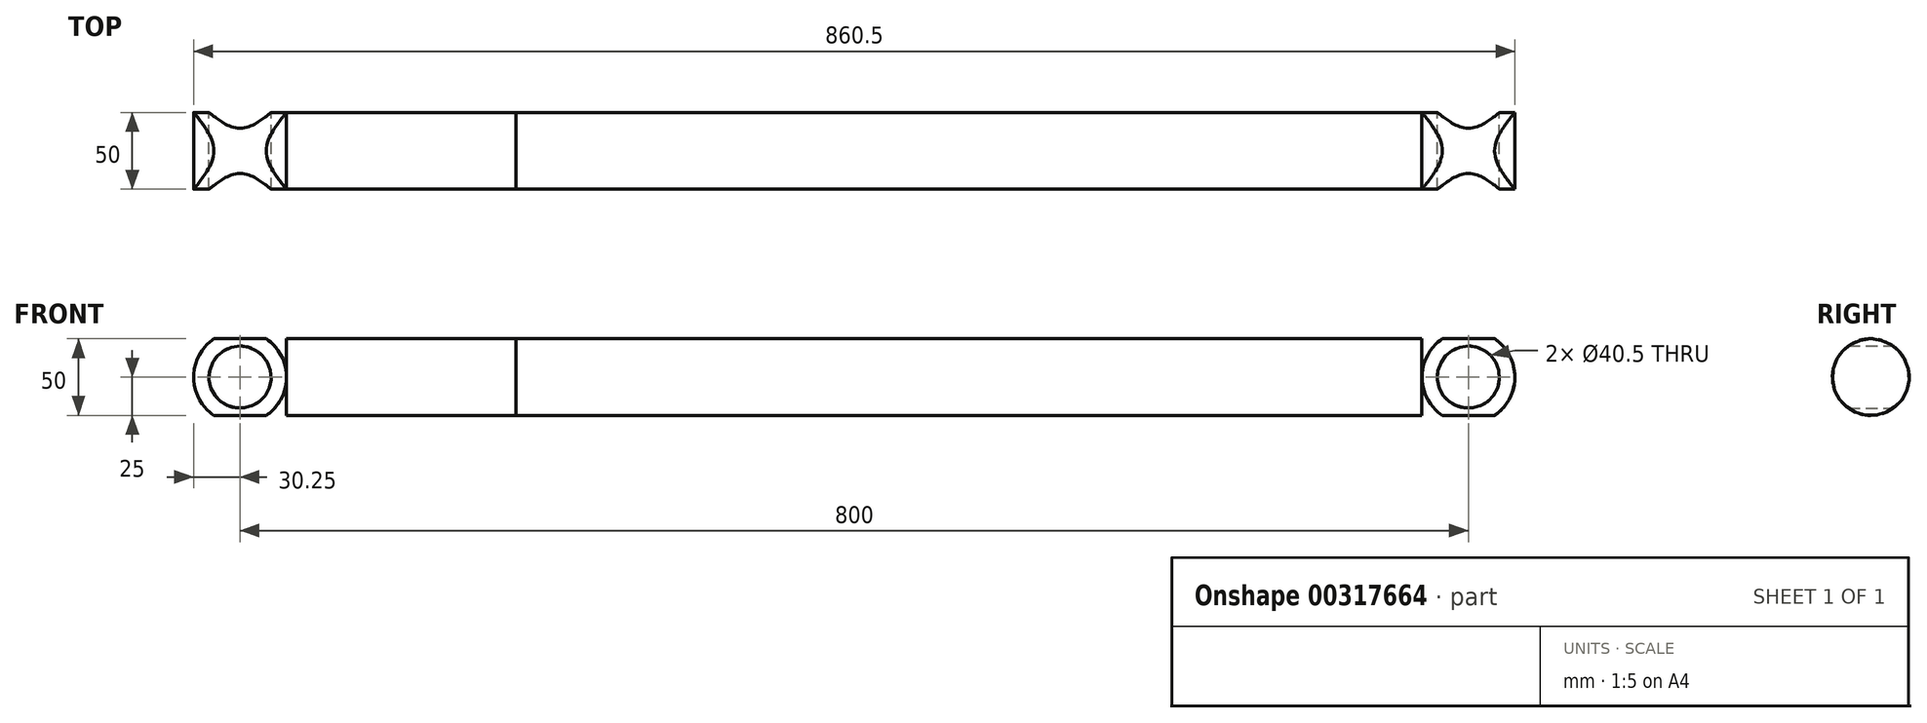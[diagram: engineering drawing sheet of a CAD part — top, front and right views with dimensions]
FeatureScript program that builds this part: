
annotation { "Feature Type Name" : "Feature", "Feature Type Description" : "" }
export const myFeature = defineFeature(function(context is Context, id is Id, definition is map)
    precondition{}
    {
        {
            assignVariable(context, id + "F0", {"name" : "Interasse_pistone", "anyValue" : 800});
        }
        {
            assignVariable(context, id + "F1", {"name" : "Corsa_persa", "anyValue" : 230});
        }
        {
            var Q0;
            Q0=qCreatedBy(makeId("Front.planeOp"),FACE);
            var sketch = newSketch(context, id + "F2", { "sketchPlane" : qUnion([Q0])});
            skCircle(sketch, "E0", {"center": v(0, 0) * mm, "radius": 20.25 * mm});
            skCircle(sketch, "E1.0", {"center": v(0, 0) * mm, "radius": 30.25 * mm});
            skLineSegment(sketch, "E2", {"start": v(0, 0) * mm, "end": v(30.25, 0) * mm, "construction": true});
            skLineSegment(sketch, "E3.bottom", {"start": v(30.25, 50) * mm, "end": v(749.75, 50) * mm});
            skLineSegment(sketch, "E3.top", {"start": v(30.25, -50) * mm, "end": v(749.75, -50) * mm});
            skLineSegment(sketch, "E3.left", {"start": v(30.25, 50) * mm, "end": v(30.25, -50) * mm});
            skLineSegment(sketch, "E3.right", {"start": v(749.75, 50) * mm, "end": v(749.75, -50) * mm});
            skLineSegment(sketch, "E4", {"start": v(30.25, 0) * mm, "end": v(749.75, 0) * mm, "construction": true});
            skCircle(sketch, "E5", {"center": v(800, 0) * mm, "radius": 20.25 * mm, "construction": true});
            skCircle(sketch, "E6.0", {"center": v(800, 0) * mm, "radius": 30.25 * mm, "construction": true});
            skLineSegment(sketch, "E7", {"start": v(769.75, 0) * mm, "end": v(830.25, 0) * mm, "construction": true});
            skLineSegment(sketch, "E8", {"start": v(800, 30.25) * mm, "end": v(800, -30.25) * mm, "construction": true});
            skLineSegment(sketch, "E9.bottom", {"start": v(830.25, 30.25) * mm, "end": v(769.75, 30.25) * mm, "construction": true});
            skLineSegment(sketch, "E9.top", {"start": v(830.25, -30.25) * mm, "end": v(769.75, -30.25) * mm, "construction": true});
            skLineSegment(sketch, "E9.left", {"start": v(830.25, 30.25) * mm, "end": v(830.25, -30.25) * mm, "construction": true});
            skLineSegment(sketch, "E9.right", {"start": v(769.75, 30.25) * mm, "end": v(769.75, -30.25) * mm, "construction": true});
            skSolve(sketch);
        }
        {
            var Q0;
            Q0=qCreatedBy(makeId("Right.planeOp"),FACE);
            var sketch = newSketch(context, id + "F3", { "sketchPlane" : qUnion([Q0])});
            skLineSegment(sketch, "E10.0", {"start": v(0, 50) * mm, "end": v(0, -50) * mm, "construction": true});
            skCircle(sketch, "E11", {"center": v(0, 0) * mm, "radius": 50 * mm});
            skSolve(sketch);
        }
        {
            var Q0;
            Q0=qCreatedBy(makeId("Right.planeOp"),FACE);
            var sketch = newSketch(context, id + "F4", { "sketchPlane" : qUnion([Q0])});
            skLineSegment(sketch, "E12.0", {"start": v(0, -30.25) * mm, "end": v(0, 30.25) * mm, "construction": true});
            skLineSegment(sketch, "E13.bottom", {"start": v(60, 30.25) * mm, "end": v(-60, 30.25) * mm});
            skLineSegment(sketch, "E13.top", {"start": v(60, -30.25) * mm, "end": v(-60, -30.25) * mm});
            skLineSegment(sketch, "E13.left", {"start": v(60, 30.25) * mm, "end": v(60, -30.25) * mm});
            skLineSegment(sketch, "E13.right", {"start": v(-60, 30.25) * mm, "end": v(-60, -30.25) * mm});
            skLineSegment(sketch, "E14", {"start": v(0, 30.25) * mm, "end": v(0, -30.25) * mm, "construction": true});
            skSolve(sketch);
        }
        {
            var Q0;
            Q0=qSketchRegion(id+"F2",true);
            extrude(context, id + "F5", {"entities" : qUnion([Q0]), "depth" : 1000 * mm, "hasSecondDirection" : true, "secondDirectionOppositeDirection" : true, "secondDirectionDepth" : 1000 * mm});
        }
        {
            var Q0;
            Q0=qSketchRegion(id+"F3",true);
            extrude(context, id + "F6", {"entities" : qUnion([Q0]), "operationType" : NewBodyOperationType.INTERSECT, "endBound" : BoundingType.THROUGH_ALL, "depth" : 25 * mm, "hasSecondDirection" : true, "secondDirectionBound" : SecondDirectionBoundingType.THROUGH_ALL, "secondDirectionOppositeDirection" : true, "secondDirectionDepth" : 25 * mm});
        }
        {
            var Q0;
            Q0=qSketchRegion(id+"F4",true);
            extrude(context, id + "F7", {"entities" : qUnion([Q0]), "operationType" : NewBodyOperationType.INTERSECT, "endBound" : BoundingType.THROUGH_ALL, "depth" : 25 * mm, "hasSecondDirection" : true, "secondDirectionBound" : SecondDirectionBoundingType.THROUGH_ALL, "secondDirectionOppositeDirection" : true, "secondDirectionDepth" : 25 * mm});
        }
        {
            var Q0;
            Q0=makeQuery(id+"F5.opExtrude","SWEPT_FACE",FACE,{"disambiguationData":[OSD([sQuery(id+"F2.wireOp",EDGE,"E3.right")])]});
            var sketch = newSketch(context, id + "F8", { "sketchPlane" : qUnion([Q0])});
            skCircle(sketch, "E15.0", {"center": v(0, 0) * mm, "radius": 50 * mm, "construction": true});
            skCircle(sketch, "E16", {"center": v(0, 0) * mm, "radius": 25 * mm});
            skSolve(sketch);
        }
        {
            var Q0;
            Q0=qSketchRegion(id+"F8",true);
            var Q1;
            Q1=makeQuery(id+"F5.opExtrude","SWEPT_FACE",FACE,{"disambiguationData":[OSD([sQuery(id+"F2.wireOp",EDGE,"E3.left")])]});
            extrude(context, id + "F9", {"entities" : qUnion([Q0]), "operationType" : NewBodyOperationType.REMOVE, "oppositeDirection" : true, "endBoundEntityFace" : qUnion([Q1]), "depth" : (getVariable(context, 'Interasse_pistone') - getVariable(context, 'Corsa_persa')) * mm});
        }
        {
            var Q0;
            Q0=qCreatedBy(makeId("Front.planeOp"),FACE);
            var sketch = newSketch(context, id + "F10", { "sketchPlane" : qUnion([Q0])});
            skCircle(sketch, "E17.0", {"center": v(800, 0) * mm, "radius": 20.25 * mm});
            skCircle(sketch, "E17.1", {"center": v(800, 0) * mm, "radius": 30.25 * mm});
            skLineSegment(sketch, "E18.bottom", {"start": v(179.75, 25) * mm, "end": v(769.75, 25) * mm});
            skLineSegment(sketch, "E18.top", {"start": v(179.75, -25) * mm, "end": v(769.75, -25) * mm});
            skLineSegment(sketch, "E18.left", {"start": v(179.75, 25) * mm, "end": v(179.75, -25) * mm});
            skLineSegment(sketch, "E18.right", {"start": v(769.75, 25) * mm, "end": v(769.75, -25) * mm});
            skLineSegment(sketch, "E19", {"start": v(179.75, 0) * mm, "end": v(769.75, 0) * mm, "construction": true});
            skSolve(sketch);
        }
        {
            var Q0;
            Q0=qCreatedBy(makeId("Right.planeOp"),FACE);
            var sketch = newSketch(context, id + "F11", { "sketchPlane" : qUnion([Q0])});
            skLineSegment(sketch, "E20.0", {"start": v(0, 25) * mm, "end": v(0, -25) * mm, "construction": true});
            skCircle(sketch, "E21", {"center": v(0, 0) * mm, "radius": 25 * mm});
            skSolve(sketch);
        }
        {
            var Q0;
            Q0=qCreatedBy(makeId("Right.planeOp"),FACE);
            var sketch = newSketch(context, id + "F12", { "sketchPlane" : qUnion([Q0])});
            skLineSegment(sketch, "E22.0", {"start": v(0, -30.25) * mm, "end": v(0, 30.25) * mm, "construction": true});
            skLineSegment(sketch, "E23.bottom", {"start": v(-60, 30.25) * mm, "end": v(60, 30.25) * mm});
            skLineSegment(sketch, "E23.top", {"start": v(-60, -30.25) * mm, "end": v(60, -30.25) * mm});
            skLineSegment(sketch, "E23.left", {"start": v(-60, 30.25) * mm, "end": v(-60, -30.25) * mm});
            skLineSegment(sketch, "E23.right", {"start": v(60, 30.25) * mm, "end": v(60, -30.25) * mm});
            skPoint(sketch, "E23.middle", {"position": v(0, 0) * mm});
            skSolve(sketch);
        }
        {
            var Q0;
            Q0=qSketchRegion(id+"F10",true);
            extrude(context, id + "F13", {"entities" : qUnion([Q0]), "depth" : 1000 * mm, "hasSecondDirection" : true, "secondDirectionOppositeDirection" : true, "secondDirectionDepth" : 1000 * mm});
        }
        {
            var Q0;
            Q0=qSketchRegion(id+"F11",true);
            extrude(context, id + "F14", {"entities" : qUnion([Q0]), "operationType" : NewBodyOperationType.INTERSECT, "endBound" : BoundingType.THROUGH_ALL, "depth" : 25 * mm, "hasSecondDirection" : true, "secondDirectionBound" : SecondDirectionBoundingType.THROUGH_ALL, "secondDirectionOppositeDirection" : true, "secondDirectionDepth" : 25 * mm});
        }
        {
            var Q0;
            Q0=qSketchRegion(id+"F12",true);
            extrude(context, id + "F15", {"entities" : qUnion([Q0]), "operationType" : NewBodyOperationType.INTERSECT, "endBound" : BoundingType.THROUGH_ALL, "depth" : 25 * mm, "hasSecondDirection" : true, "secondDirectionBound" : SecondDirectionBoundingType.THROUGH_ALL, "secondDirectionOppositeDirection" : true, "secondDirectionDepth" : 25 * mm});
        }
    });
